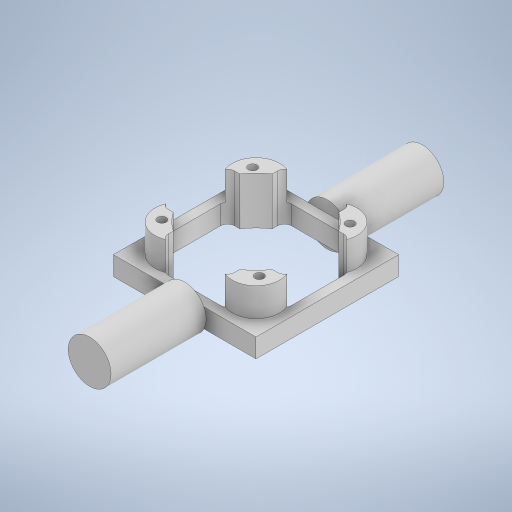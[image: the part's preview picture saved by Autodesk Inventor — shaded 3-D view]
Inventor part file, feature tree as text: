
AUTODESK INVENTOR PART (.ipt)
format: ipt  version: 2024 (Build 280153000, 153)  size: 433,664 bytes
history: native  units: in
note: dims shown in document units (in); Inventor stores cm internally (conversion verified against a paired STEP export)
features: extrude x8, sketch x8, fillet x1
ambient origin geometry x8: Origin, YZ Plane, XZ Plane, XY Plane, X Axis, Y Axis, Z Axis, Center Point
bodies: Solid1 (feature_tree)
feature tree (17):
  extrude  "Extrusion1"  Depth=3.937in TaperAngle=0.0deg
  sketch  "Sketch2"  dims[d3=1.378in d32=5.9055in]
  extrude  "Extrusion5"  Depth=5.9055in
  extrude  "Extrusion8"  Depth=5.9055in TaperAngle=0.0deg
  extrude  "Extrusion10"  Depth=5.1181in
  extrude  "Extrusion11"  Depth=5.1181in
  extrude  "Extrusion12"  Depth=0.7874in TaperAngle=0.0deg
  extrude  "Extrusion13"  Depth=1.378in
  extrude  "Extrusion14"  Depth=0.3in
  fillet  "Fillet7"  Radius=1.378in
  sketch  "Sketch1"  dims[d0=1.7717in d1=3.937in d2=0.0in]
  sketch  "Sketch5"  dims[d33=0.7874in d34=5.9055in d35=0.0in]
  sketch  "Sketch8"  dims[d59=3.937in d60=0.0in d72=5.1181in]
  sketch  "Sketch11"  dims[d73=5.1181in d74=2.9528in]
  sketch  "Sketch12"  dims[d75=2.9528in d80=0.7874in d81=0.0in]
  sketch  "Sketch13"  dims[d84=1.378in d85=1.378in]
  sketch  "Sketch14"  dims[d86=0.5118in d87=1.378in d88=1.378in d89=0.5118in d90=2.5315in d91=0.3543in d92=0.5026in d93=0.5407in d94=1.9685in d95=0.0in d96=1.378in d97=1.378in d98=1.378in d99=1.378in d100=0.5118in d101=0.5118in d102=0.5118in d103=0.5118in d104=0.5118in d105=0.5118in d106=2.5315in d107=2.5315in d108=2.5315in d109=0.3543in d110=0.3543in d111=0.3543in d112=0.5026in d113=0.5407in d114=0.5026in d115=0.5407in d116=0.5407in d117=0.5026in d118=0.9843in d119=0.9843in d120=0.9843in d121=0.9843in d122=2.5315in d125=2.5315in d126=2.5315in d127=2.5315in d128=1.1811in d129=0.0in d130=0.3543in d131=0.3543in d132=0.3543in d133=0.3543in d134=3.937in d135=0.0in d136=1.7717in d144=2.9921in d145=0.0in d148=0.3in d28=0.0in d29=0.0in d30=0.0in d31=0.0in d146=0.0197in d147=0.0344in]
